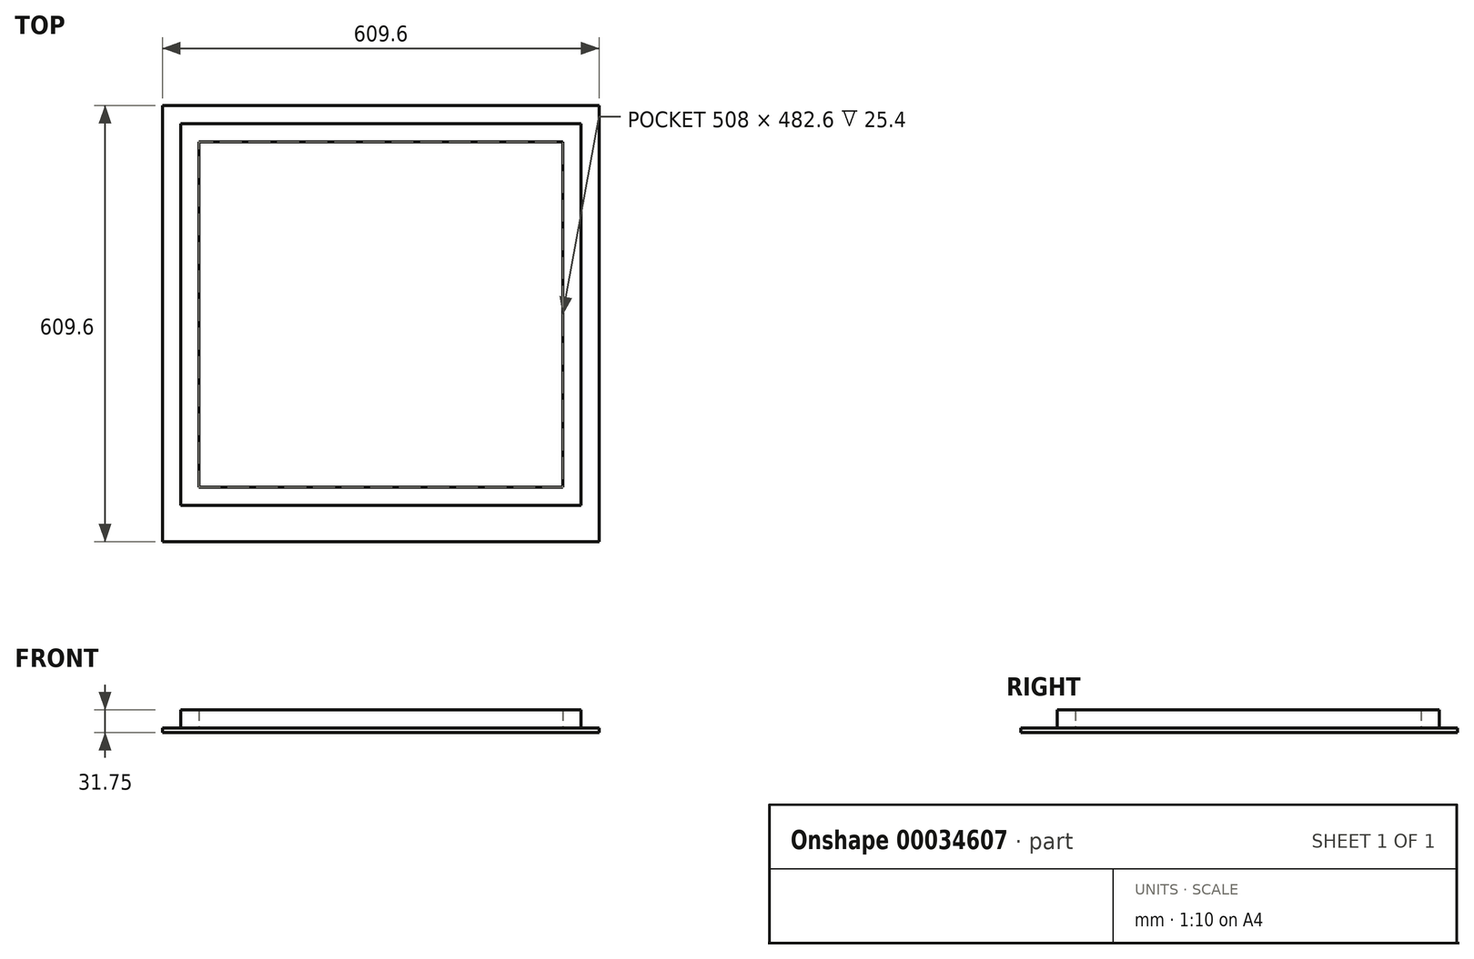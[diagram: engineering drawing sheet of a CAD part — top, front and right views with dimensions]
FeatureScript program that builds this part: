
annotation { "Feature Type Name" : "Feature", "Feature Type Description" : "" }
export const myFeature = defineFeature(function(context is Context, id is Id, definition is map)
    precondition{}
    {
        {
            var Q0;
            Q0=qCreatedBy(makeId("Top.planeOp"),FACE);
            var sketch = newSketch(context, id + "F0", { "sketchPlane" : qUnion([Q0])});
            skLineSegment(sketch, "E0.bottom", {"start": v(0, 0) * mm, "end": v(609.6, 0) * mm});
            skLineSegment(sketch, "E0.top", {"start": v(0, -609.6) * mm, "end": v(609.6, -609.6) * mm});
            skLineSegment(sketch, "E0.left", {"start": v(0, 0) * mm, "end": v(0, -609.6) * mm});
            skLineSegment(sketch, "E0.right", {"start": v(609.6, 0) * mm, "end": v(609.6, -609.6) * mm});
            skSolve(sketch);
        }
        {
            var Q0;
            Q0=qSketchRegion(id+"F0",true);
            extrude(context, id + "F1", {"entities" : qUnion([Q0]), "depth" : 6.35 * mm});
        }
        {
            var Q0;
            Q0=makeQuery(id+"F1.opExtrude","CAP_FACE",FACE,{"disambiguationData":[OSD([sQuery(id+"F0.wireOp",EDGE,"E0.bottom"),sQuery(id+"F0.wireOp",EDGE,"E0.top"),sQuery(id+"F0.wireOp",EDGE,"E0.left"),sQuery(id+"F0.wireOp",EDGE,"E0.right")])],"isStart":false});
            var sketch = newSketch(context, id + "F2", { "sketchPlane" : qUnion([Q0])});
            skLineSegment(sketch, "E1.bottom", {"start": v(25.4, -25.4) * mm, "end": v(584.2, -25.4) * mm});
            skLineSegment(sketch, "E1.top", {"start": v(25.4, -558.8) * mm, "end": v(584.2, -558.8) * mm});
            skLineSegment(sketch, "E1.left", {"start": v(25.4, -25.4) * mm, "end": v(25.4, -558.8) * mm});
            skLineSegment(sketch, "E1.right", {"start": v(584.2, -25.4) * mm, "end": v(584.2, -558.8) * mm});
            skLineSegment(sketch, "E2.bottom", {"start": v(50.8, -533.4) * mm, "end": v(558.8, -533.4) * mm});
            skLineSegment(sketch, "E2.top", {"start": v(50.8, -50.8) * mm, "end": v(558.8, -50.8) * mm});
            skLineSegment(sketch, "E2.left", {"start": v(50.8, -533.4) * mm, "end": v(50.8, -50.8) * mm});
            skLineSegment(sketch, "E2.right", {"start": v(558.8, -533.4) * mm, "end": v(558.8, -50.8) * mm});
            skSolve(sketch);
        }
        {
            var Q0;
            Q0 = qSketchRegion(id + "F2", true);
            extrude(context, id + "F3", {"entities" : qUnion([Q0]), "operationType" : NewBodyOperationType.ADD, "depth" : 25.4 * mm});
        }
    });
